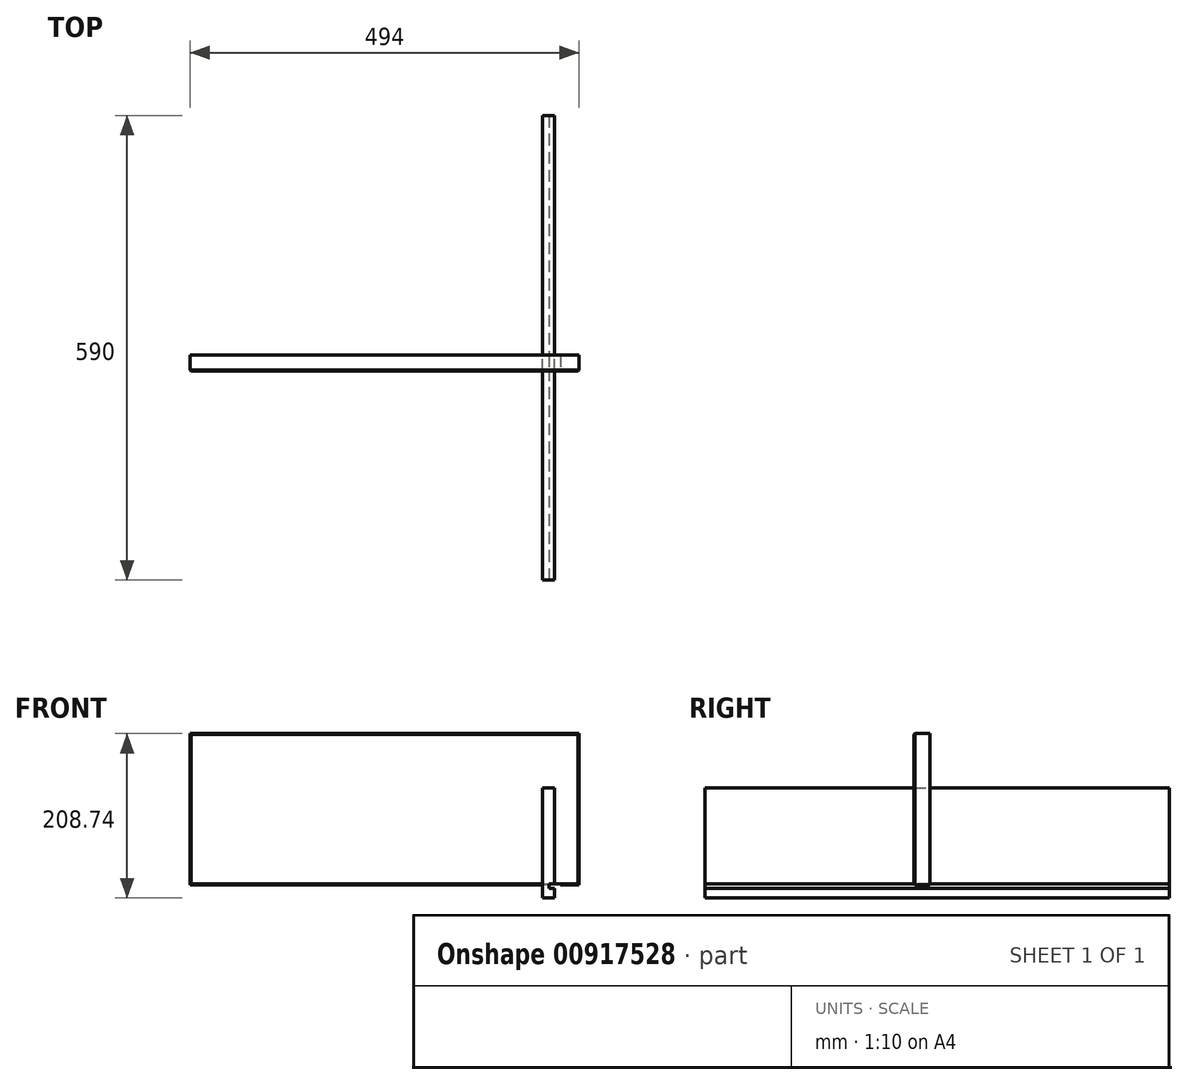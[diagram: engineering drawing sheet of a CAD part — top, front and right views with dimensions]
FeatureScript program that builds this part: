
annotation { "Feature Type Name" : "Feature", "Feature Type Description" : "" }
export const myFeature = defineFeature(function(context is Context, id is Id, definition is map)
    precondition{}
    {
        {
            var Q0;
            Q0=qCreatedBy(makeId("Front.planeOp"),FACE);
            var sketch = newSketch(context, id + "F0", { "sketchPlane" : qUnion([Q0])});
            skLineSegment(sketch, "E0.bottom", {"start": v(-447.82, 168.68) * mm, "end": v(46.18, 168.68) * mm});
            skLineSegment(sketch, "E0.top", {"start": v(-447.82, -23.32) * mm, "end": v(46.18, -23.32) * mm});
            skLineSegment(sketch, "E0.left", {"start": v(-447.82, 168.68) * mm, "end": v(-447.82, -23.32) * mm});
            skLineSegment(sketch, "E0.right", {"start": v(46.18, 168.68) * mm, "end": v(46.18, -23.32) * mm});
            skSolve(sketch);
        }
        {
            var Q0;
            Q0 = qSketchRegion(id + "F0", true);
            extrude(context, id + "F1", {"entities" : qUnion([Q0]), "depth" : 20 * mm, "offsetDistance" : 25 * mm});
        }
        {
            var Q0;
            Q0=makeQuery(id+"F1.opExtrude","CAP_EDGE",EDGE,{"disambiguationData":[OSD([sQuery(id+"F0.wireOp",EDGE,"E0.top")])],"isStart":false});
            var Q1;
            Q1=makeQuery(id+"F1.opExtrude","CAP_FACE",FACE,{"disambiguationData":[OSD([sQuery(id+"F0.wireOp",EDGE,"E0.bottom"),sQuery(id+"F0.wireOp",EDGE,"E0.top"),sQuery(id+"F0.wireOp",EDGE,"E0.left"),sQuery(id+"F0.wireOp",EDGE,"E0.right")])],"isStart":false});
            chamfer(context, id + "F2", {"entities" : qUnion([Q0, Q1]), "width" : 1 * mm, "tangentPropagation" : true});
        }
        {
            var Q0;
            Q0=qCreatedBy(makeId("Right.planeOp"),FACE);
            var sketch = newSketch(context, id + "F3", { "sketchPlane" : qUnion([Q0])});
            skLineSegment(sketch, "E1.bottom", {"start": v(-285.75, 99.94) * mm, "end": v(304.25, 99.94) * mm});
            skLineSegment(sketch, "E1.top", {"start": v(-285.75, -40.06) * mm, "end": v(304.25, -40.06) * mm});
            skLineSegment(sketch, "E1.left", {"start": v(-285.75, 99.94) * mm, "end": v(-285.75, -40.06) * mm});
            skLineSegment(sketch, "E1.right", {"start": v(304.25, 99.94) * mm, "end": v(304.25, -40.06) * mm});
            skSolve(sketch);
        }
        {
            var Q0;
            Q0 = qSketchRegion(id + "F3", true);
            extrude(context, id + "F4", {"entities" : qUnion([Q0]), "depth" : 15 * mm, "offsetDistance" : 25 * mm});
        }
        {
            var Q0;
            Q0=makeQuery(id+"F4.opExtrude","SWEPT_FACE",FACE,{"disambiguationData":[OSD([sQuery(id+"F3.wireOp",EDGE,"E1.left")])]});
            var sketch = newSketch(context, id + "F5", { "sketchPlane" : qUnion([Q0])});
            skLineSegment(sketch, "E2.bottom", {"start": v(23, -22.06) * mm, "end": v(8, -22.06) * mm});
            skLineSegment(sketch, "E2.top", {"start": v(23, -28.06) * mm, "end": v(8, -28.06) * mm});
            skLineSegment(sketch, "E2.left", {"start": v(23, -22.06) * mm, "end": v(23, -28.06) * mm});
            skLineSegment(sketch, "E2.right", {"start": v(8, -22.06) * mm, "end": v(8, -28.06) * mm});
            skSolve(sketch);
        }
        {
            var Q0;
            Q0 = qSketchRegion(id + "F5", true);
            extrude(context, id + "F6", {"entities" : qUnion([Q0]), "operationType" : NewBodyOperationType.REMOVE, "oppositeDirection" : true, "depth" : 800 * mm, "offsetDistance" : 25 * mm});
        }
    });
